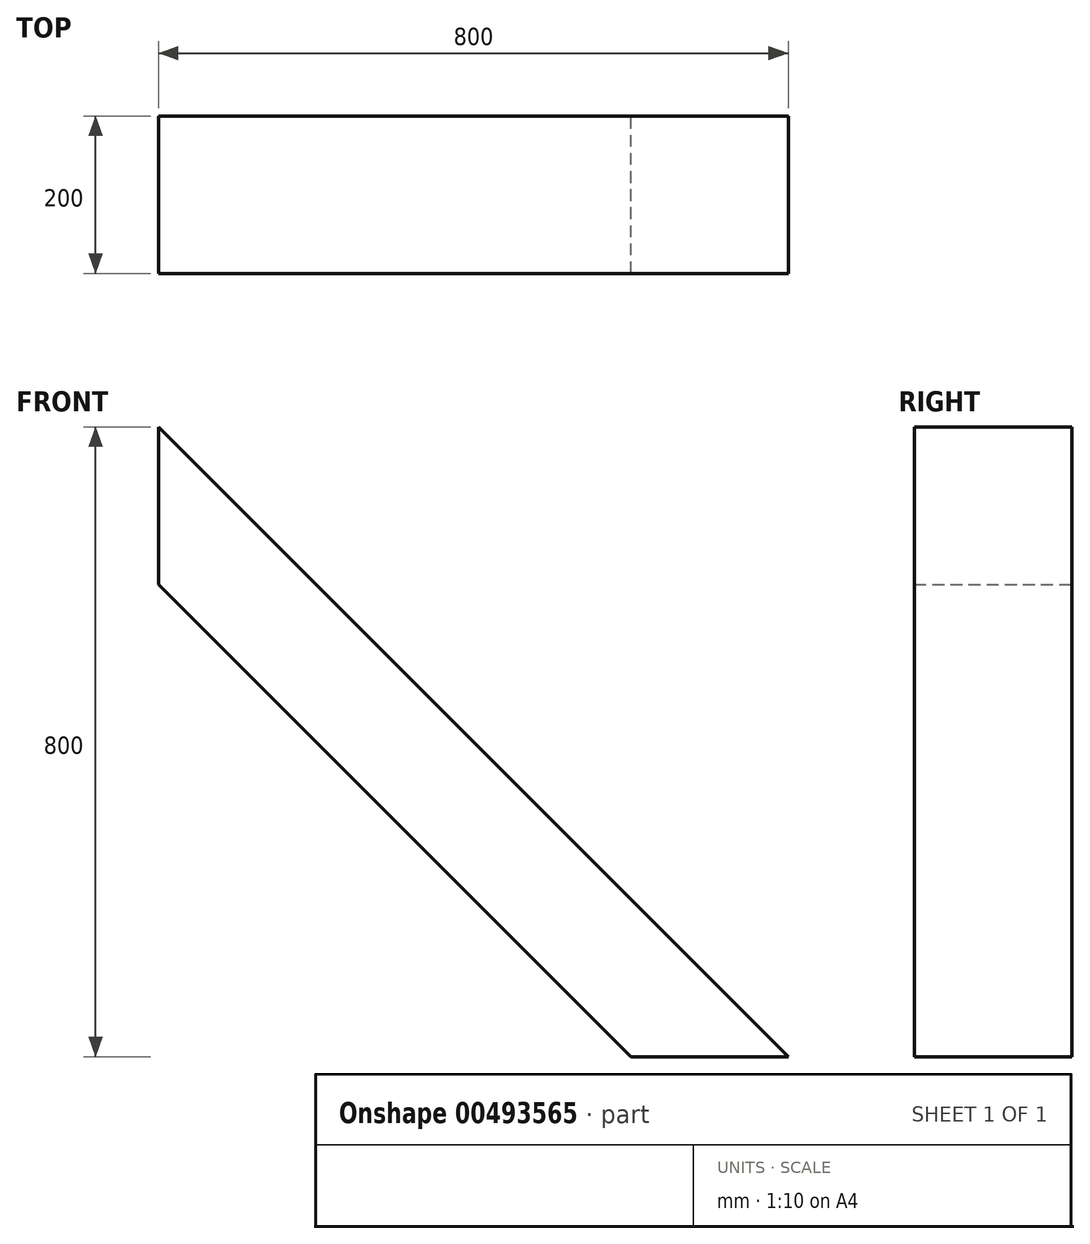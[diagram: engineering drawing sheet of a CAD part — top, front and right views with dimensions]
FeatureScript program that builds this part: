
annotation { "Feature Type Name" : "Feature", "Feature Type Description" : "" }
export const myFeature = defineFeature(function(context is Context, id is Id, definition is map)
    precondition{}
    {
        {
            var Q0;
            Q0=qCreatedBy(makeId("Front.planeOp"),FACE);
            var sketch = newSketch(context, id + "F0", { "sketchPlane" : qUnion([Q0])});
            skLineSegment(sketch, "E0", {"start": v(0, 800) * mm, "end": v(0, 600) * mm});
            skLineSegment(sketch, "E1", {"start": v(600, 0) * mm, "end": v(800, 0) * mm});
            skLineSegment(sketch, "E2", {"start": v(0, 800) * mm, "end": v(800, 0) * mm});
            skPoint(sketch, "E3", {"position": v(0, 600) * mm});
            skPoint(sketch, "E4", {"position": v(600, 0) * mm});
            skLineSegment(sketch, "E5", {"start": v(0, 600) * mm, "end": v(600, 0) * mm});
            skSolve(sketch);
        }
        {
            var Q0;
            Q0 = qSketchRegion(id + "F0", true);
            extrude(context, id + "F1", {"entities" : qUnion([Q0]), "endBound" : BoundingType.SYMMETRIC, "depth" : 200 * mm});
        }
    });
